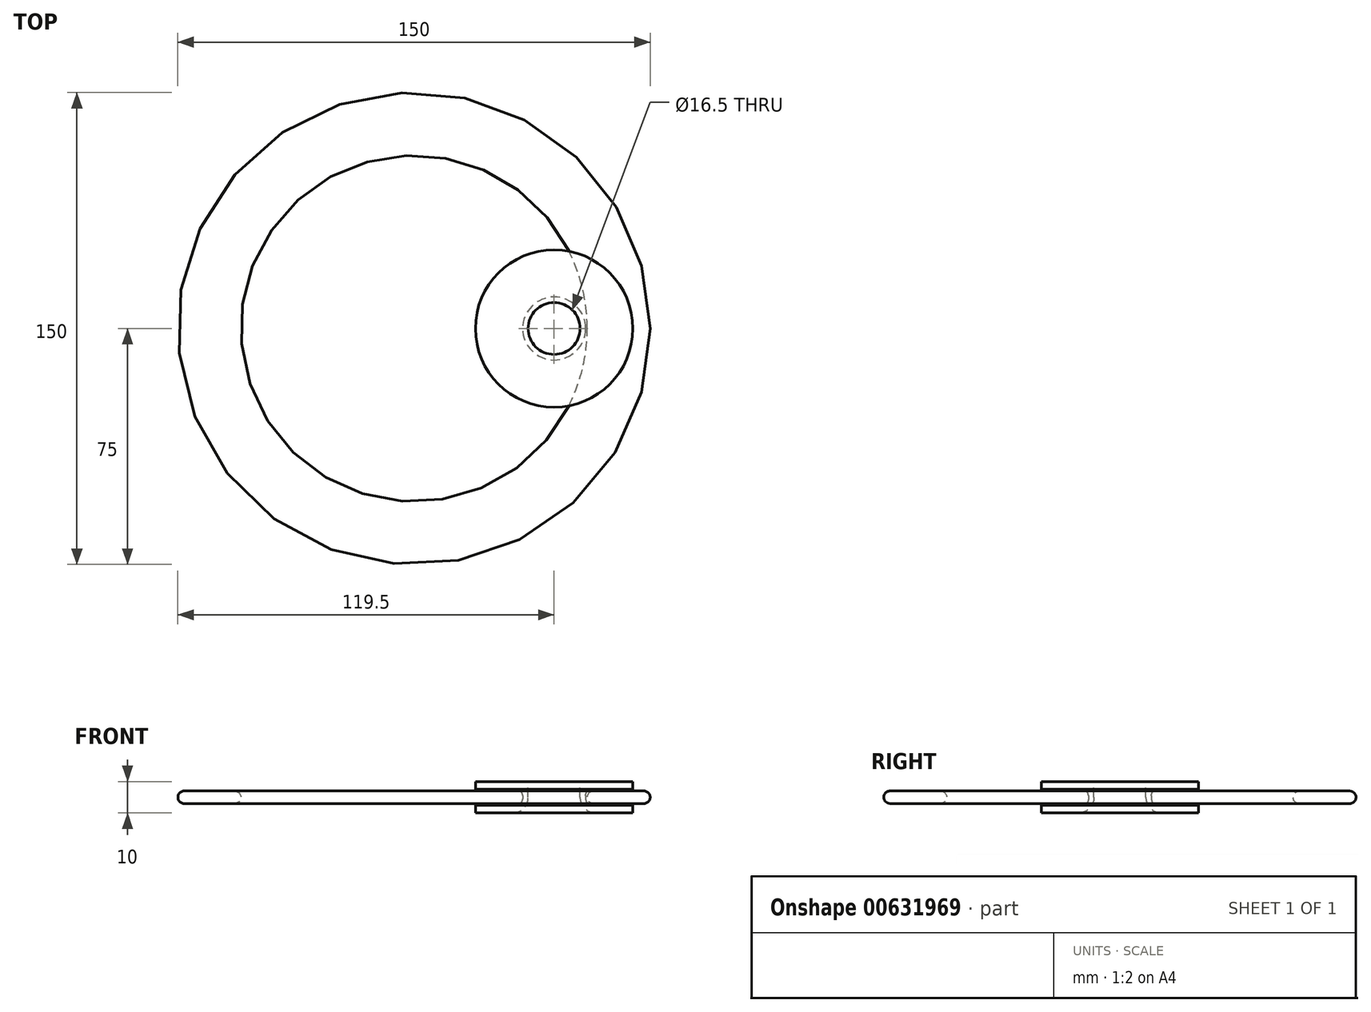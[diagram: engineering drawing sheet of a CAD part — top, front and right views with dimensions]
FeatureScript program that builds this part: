
annotation { "Feature Type Name" : "Feature", "Feature Type Description" : "" }
export const myFeature = defineFeature(function(context is Context, id is Id, definition is map)
    precondition{}
    {
        {
            var Q0;
            Q0=qCreatedBy(makeId("Top.planeOp"),FACE);
            var sketch = newSketch(context, id + "F0", { "sketchPlane" : qUnion([Q0])});
            skCircle(sketch, "E0", {"center": v(0, 0) * mm, "radius": 55 * mm});
            skCircle(sketch, "E1.0", {"center": v(0, 0) * mm, "radius": 75 * mm});
            skSolve(sketch);
        }
        {
            var Q0;
            Q0=makeQuery(id+"F0.imprint","IMPRINT",FACE,{"disambiguationData":[TD([[makeQuery(id+"F0.imprint","IMPRINT",EDGE,{"derivedFrom":sQuery(id+"F0.wireOp",EDGE,"E0")}),-1.0]])]});
            extrude(context, id + "F1", {"entities" : qUnion([Q0]), "depth" : 4 * mm, "offsetDistance" : 25 * mm});
        }
        {
            var Q0;
            Q0=qCreatedBy(makeId("Front.planeOp"),FACE);
            var sketch = newSketch(context, id + "F2", { "sketchPlane" : qUnion([Q0])});
            skLineSegment(sketch, "E2", {"start": v(55, 14.12) * mm, "end": v(55, -7.03) * mm, "construction": true});
            skLineSegment(sketch, "E3", {"start": v(75, -7.47) * mm, "end": v(75, 11.99) * mm, "construction": true});
            skLineSegment(sketch, "E4", {"start": v(54.5, 4.5) * mm, "end": v(54.5, -0.5) * mm});
            skLineSegment(sketch, "E5", {"start": v(54.5, 7) * mm, "end": v(69.5, 7) * mm});
            skLineSegment(sketch, "E6", {"start": v(54.5, -3) * mm, "end": v(69.5, -3) * mm});
            skLineSegment(sketch, "E7", {"start": v(54.5, 4.5) * mm, "end": v(69.5, 4.5) * mm});
            skLineSegment(sketch, "E8", {"start": v(54.5, -0.5) * mm, "end": v(69.5, -0.5) * mm});
            skLineSegment(sketch, "E9", {"start": v(69.5, 4.5) * mm, "end": v(69.5, 7) * mm});
            skLineSegment(sketch, "E10", {"start": v(69.5, -0.5) * mm, "end": v(69.5, -3) * mm});
            skLineSegment(sketch, "E11", {"start": v(44.5, -3) * mm, "end": v(44.5, 7) * mm});
            skLineSegment(sketch, "E12", {"start": v(44.5, 7) * mm, "end": v(54.5, 7) * mm});
            skLineSegment(sketch, "E13", {"start": v(44.5, -3) * mm, "end": v(54.5, -3) * mm});
            skSolve(sketch);
        }
        {
            var Q0;
            Q0=makeQuery(id+"F2.imprint","IMPRINT",FACE,{"disambiguationData":[TD([[makeQuery(id+"F2.imprint","IMPRINT",EDGE,{"derivedFrom":sQuery(id+"F2.wireOp",EDGE,"E4")}),-1.0]])]});
            var Q1;
            Q1=sQuery(id+"F2.wireOp",EDGE,"E11");
            revolve(context, id + "F3", {"entities" : qUnion([Q0]), "axis" : qUnion([Q1]), "revolveType" : RevolveType.FULL});
        }
        {
            var Q0;
            Q0=makeQuery(id+"F3.opRevolve","SWEPT_FACE",FACE,{"disambiguationData":[OSD([sQuery(id+"F2.wireOp",EDGE,"E5"),sQuery(id+"F2.wireOp",EDGE,"E12")])]});
            var sketch = newSketch(context, id + "F4", { "sketchPlane" : qUnion([Q0])});
            skCircle(sketch, "E14", {"center": v(44.5, 0) * mm, "radius": 8.25 * mm});
            skSolve(sketch);
        }
        {
            var Q0;
            Q0=makeQuery(id+"F4.imprint","IMPRINT",FACE,{"disambiguationData":[TD([[makeQuery(id+"F4.imprint","IMPRINT",EDGE,{"derivedFrom":sQuery(id+"F4.wireOp",EDGE,"E14")}),1.0]])]});
            extrude(context, id + "F5", {"entities" : qUnion([Q0]), "operationType" : NewBodyOperationType.REMOVE, "oppositeDirection" : true, "depth" : 25 * mm, "offsetDistance" : 25 * mm});
        }
        {
            var Q0;
            Q0=makeQuery(id+"F5.boolean.opBoolean","COPY",EDGE,{"derivedFrom":makeQuery(id+"F5.opExtrude","CAP_EDGE",EDGE,{"disambiguationData":[OSD([sQuery(id+"F4.wireOp",EDGE,"E14")])],"isStart":true})});
            var Q1;
            Q1=makeQuery(id+"F5.boolean.opBoolean","INTERSECT",EDGE,{"derivedFrom":[makeQuery(id+"F3.opRevolve","SWEPT_FACE",FACE,{"disambiguationData":[OSD([sQuery(id+"F2.wireOp",EDGE,"E6"),sQuery(id+"F2.wireOp",EDGE,"E13")])]}),makeQuery(id+"F5.opExtrude","SWEPT_FACE",FACE,{"disambiguationData":[OSD([sQuery(id+"F4.wireOp",EDGE,"E14")])]})]});
            fillet(context, id + "F6", {"entities" : qUnion([Q0, Q1]), "radius" : 5 * mm, "tangentPropagation" : true, "allowEdgeOverflow" : false});
        }
        {
            var Q0;
            Q0=makeQuery(id+"F1.opExtrude","SWEPT_FACE",FACE,{"disambiguationData":[OSD([sQuery(id+"F0.wireOp",EDGE,"E0")])]});
            var Q1;
            Q1=makeQuery(id+"F3.opRevolve","SWEPT_FACE",FACE,{"disambiguationData":[OSD([sQuery(id+"F2.wireOp",EDGE,"E4")])]});
            fillet(context, id + "F7", {"entities" : qUnion([Q0, Q1]), "radius" : 2 * mm, "tangentPropagation" : true, "allowEdgeOverflow" : false});
        }
        {
            var Q0;
            Q0=makeQuery(id+"F1.opExtrude","CAP_EDGE",EDGE,{"disambiguationData":[OSD([sQuery(id+"F0.wireOp",EDGE,"E1.0")])],"isStart":false});
            var Q1;
            Q1=makeQuery(id+"F1.opExtrude","CAP_EDGE",EDGE,{"disambiguationData":[OSD([sQuery(id+"F0.wireOp",EDGE,"E1.0")])],"isStart":true});
            fillet(context, id + "F8", {"entities" : qUnion([Q0, Q1]), "radius" : 2 * mm, "tangentPropagation" : true, "allowEdgeOverflow" : false});
        }
    });
